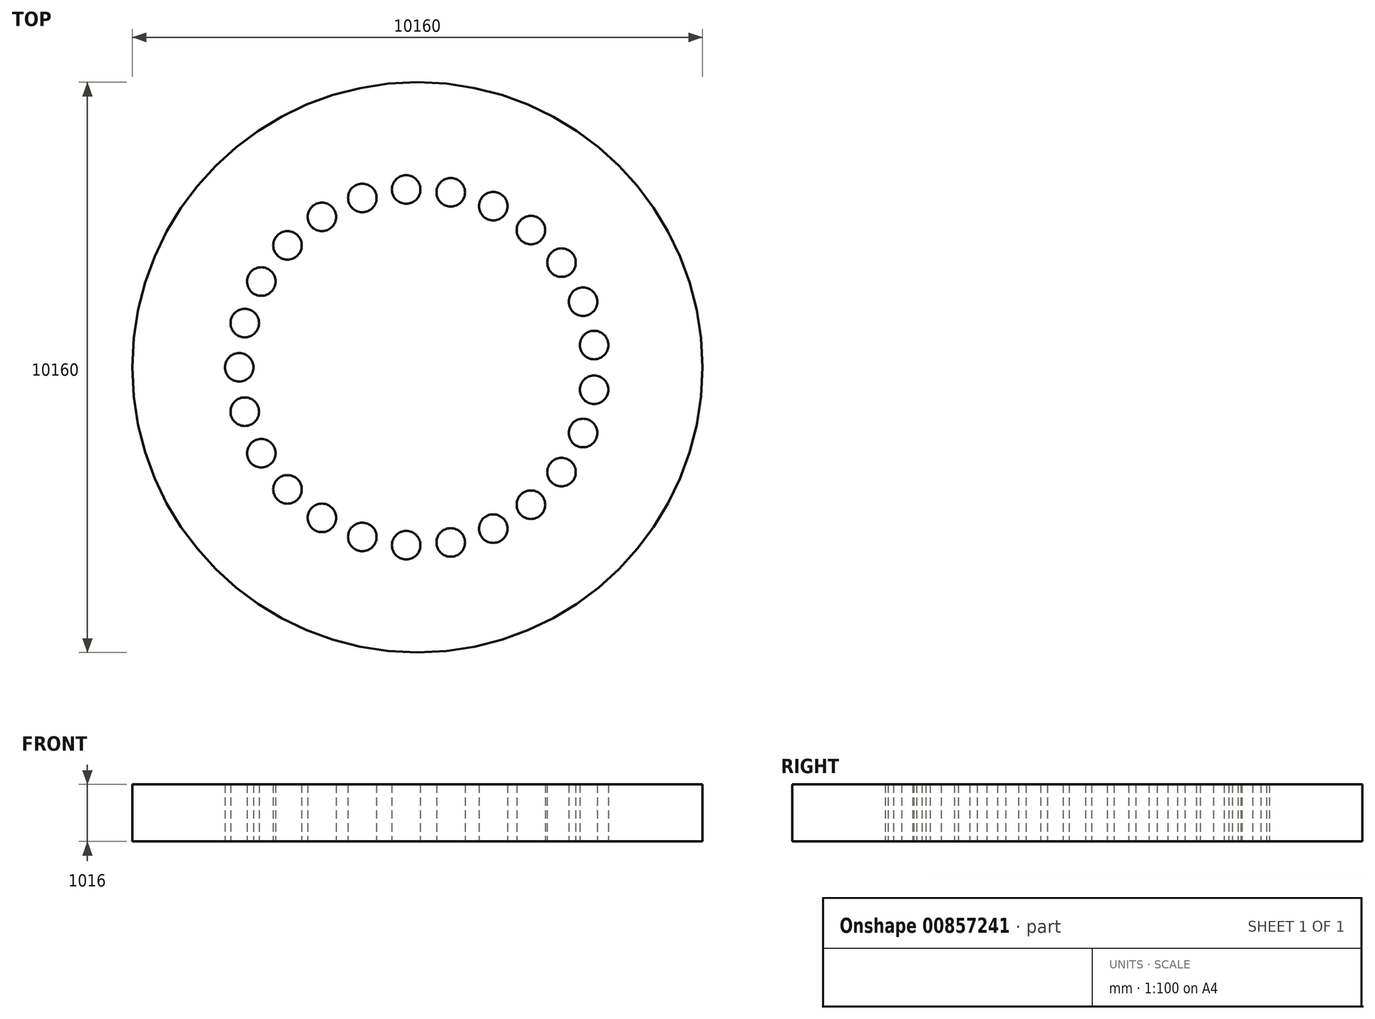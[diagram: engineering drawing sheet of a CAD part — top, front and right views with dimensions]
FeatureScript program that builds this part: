
annotation { "Feature Type Name" : "Feature", "Feature Type Description" : "" }
export const myFeature = defineFeature(function(context is Context, id is Id, definition is map)
    precondition{}
    {
        {
            var Q0;
            Q0=qCreatedBy(makeId("Top.planeOp"),FACE);
            var sketch = newSketch(context, id + "F0", { "sketchPlane" : qUnion([Q0])});
            skCircle(sketch, "E0", {"center": v(0, 0) * mm, "radius": 3175 * mm});
            skCircle(sketch, "E1", {"center": v(0, 0) * mm, "radius": 5080 * mm});
            skLineSegment(sketch, "E2", {"start": v(0, 0) * mm, "end": v(-4434.2, 0) * mm, "construction": true});
            skLineSegment(sketch, "E3", {"start": v(0, 0) * mm, "end": v(-1035.95, -3866.23) * mm, "construction": true});
            skCircle(sketch, "E4", {"center": v(-981.13, -3019.6) * mm, "radius": 254 * mm});
            skCircle(sketch, "E5.1.0", {"center": v(-199.36, -3168.73) * mm, "radius": 254 * mm});
            skCircle(sketch, "E5.2.0", {"center": v(594.94, -3118.76) * mm, "radius": 254 * mm});
            skCircle(sketch, "E5.3.0", {"center": v(1351.85, -2872.83) * mm, "radius": 254 * mm});
            skCircle(sketch, "E5.4.0", {"center": v(2023.82, -2446.38) * mm, "radius": 254 * mm});
            skCircle(sketch, "E5.5.0", {"center": v(2568.63, -1866.22) * mm, "radius": 254 * mm});
            skCircle(sketch, "E5.6.0", {"center": v(2952.04, -1168.8) * mm, "radius": 254 * mm});
            skCircle(sketch, "E5.7.0", {"center": v(3149.96, -397.93) * mm, "radius": 254 * mm});
            skCircle(sketch, "E5.8.0", {"center": v(3149.96, 397.93) * mm, "radius": 254 * mm});
            skCircle(sketch, "E5.9.0", {"center": v(2952.04, 1168.8) * mm, "radius": 254 * mm});
            skCircle(sketch, "E5.10.0", {"center": v(2568.63, 1866.22) * mm, "radius": 254 * mm});
            skCircle(sketch, "E5.11.0", {"center": v(2023.82, 2446.38) * mm, "radius": 254 * mm});
            skCircle(sketch, "E5.12.0", {"center": v(1351.85, 2872.83) * mm, "radius": 254 * mm});
            skCircle(sketch, "E5.13.0", {"center": v(594.94, 3118.76) * mm, "radius": 254 * mm});
            skCircle(sketch, "E5.14.0", {"center": v(-199.36, 3168.73) * mm, "radius": 254 * mm});
            skCircle(sketch, "E5.15.0", {"center": v(-981.13, 3019.6) * mm, "radius": 254 * mm});
            skCircle(sketch, "E5.16.0", {"center": v(-1701.25, 2680.74) * mm, "radius": 254 * mm});
            skCircle(sketch, "E5.17.0", {"center": v(-2314.48, 2173.44) * mm, "radius": 254 * mm});
            skCircle(sketch, "E5.18.0", {"center": v(-2782.27, 1529.57) * mm, "radius": 254 * mm});
            skCircle(sketch, "E5.19.0", {"center": v(-3075.25, 789.6) * mm, "radius": 254 * mm});
            skCircle(sketch, "E5.20.0", {"center": v(-3175, 0) * mm, "radius": 254 * mm});
            skCircle(sketch, "E5.21.0", {"center": v(-3075.25, -789.6) * mm, "radius": 254 * mm});
            skCircle(sketch, "E5.22.0", {"center": v(-2782.27, -1529.57) * mm, "radius": 254 * mm});
            skCircle(sketch, "E5.23.0", {"center": v(-2314.48, -2173.44) * mm, "radius": 254 * mm});
            skCircle(sketch, "E5.24.0", {"center": v(-1701.25, -2680.74) * mm, "radius": 254 * mm});
            skSolve(sketch);
        }
        {
            var Q0;
            Q0 = qSketchRegion(id + "F0", true);
            var Q1;
            {var subQ0=sQuery(id+"F0.wireOp",EDGE,"E5.8.0");var subQ1=sQuery(id+"F0.wireOp",EDGE,"E0");var subQ43=makeQuery(id+"F0.imprint","INTERSECT",VERTEX,{"disambiguationData":[OD(0.0)],"derivedFrom":[subQ1,subQ0]});Q1=makeQuery(id+"F0.imprint","IMPRINT",FACE,{"disambiguationData":[TD([[makeQuery(id+"F0.imprint","IMPRINT",EDGE,{"disambiguationData":[TD([[subQ43,-1.0]])],"derivedFrom":subQ1}),1.0]])]});}
            extrude(context, id + "F1", {"entities" : qUnion([Q0, Q1]), "endBound" : BoundingType.SYMMETRIC, "depth" : 1016 * mm, "offsetDistance" : 25.4 * mm});
        }
    });
